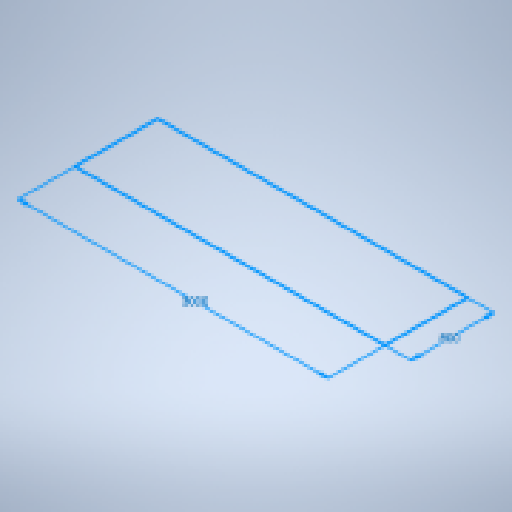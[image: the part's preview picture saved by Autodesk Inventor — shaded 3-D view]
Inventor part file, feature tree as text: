
AUTODESK INVENTOR PART (.ipt)
format: ipt  version: 2025 (Build 290162010, 162A)  size: 139,776 bytes
history: native  units: mm
features: sketch x1
ambient origin geometry x8: Origin, YZ Plane, XZ Plane, XY Plane, X Axis, Y Axis, Z Axis, Center Point
feature tree (1):
  sketch  "Sketch1"  dims[d0=3000.0mm d1=800.0mm d2=1500.0mm d14=600.0mm d15=350.0mm d16=350.0mm d17=500.0mm d18=350.0mm d20=500.0mm d21=350.0mm]
